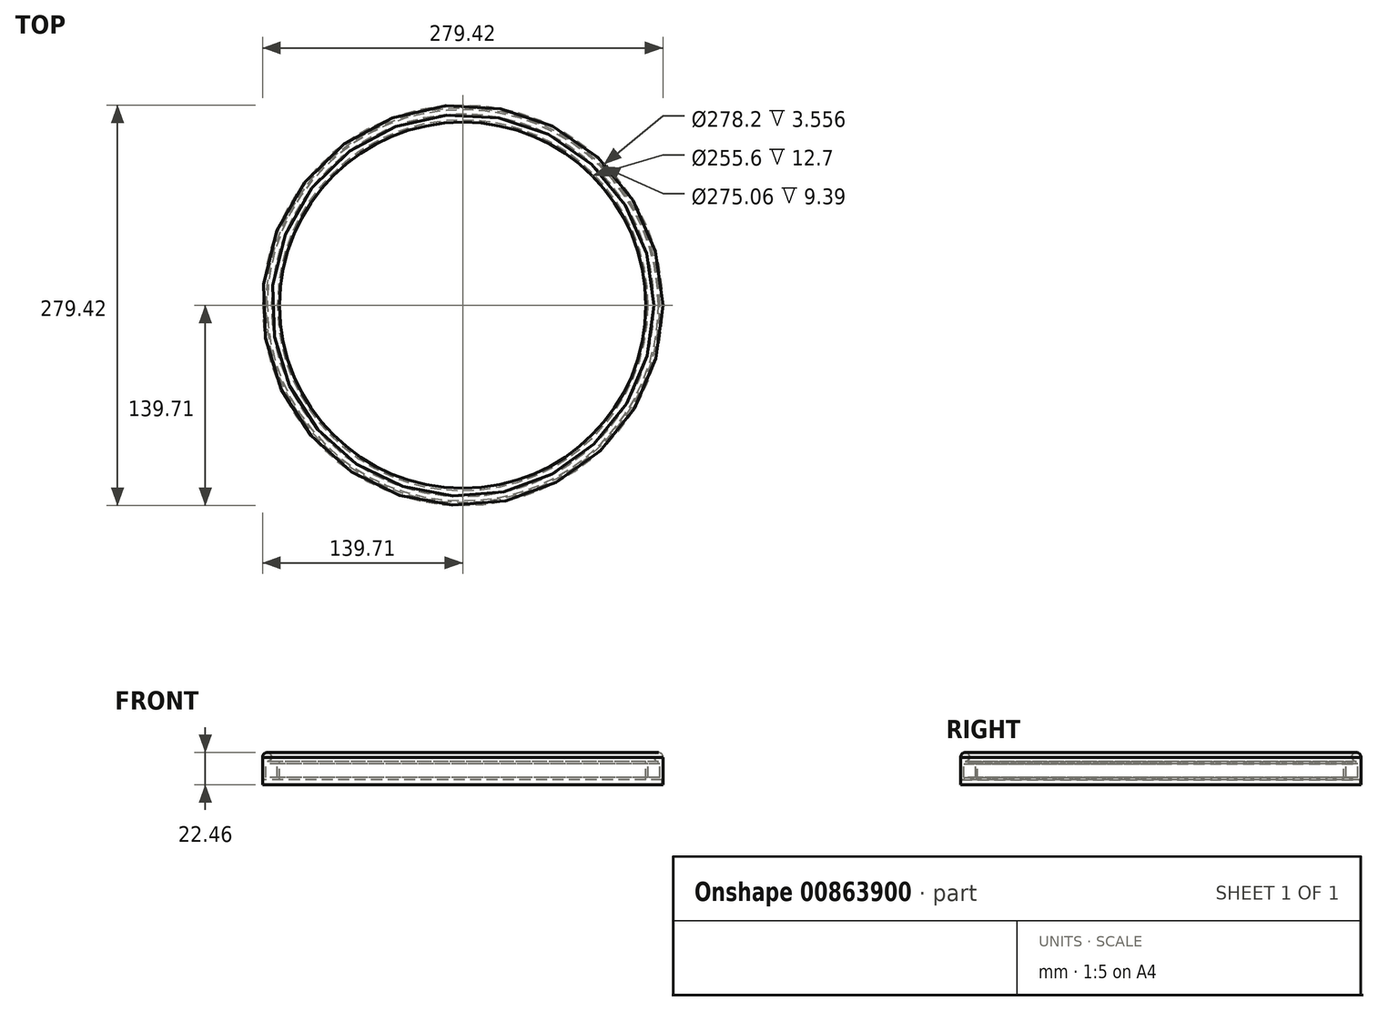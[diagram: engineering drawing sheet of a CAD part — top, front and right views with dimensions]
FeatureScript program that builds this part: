
annotation { "Feature Type Name" : "Feature", "Feature Type Description" : "" }
export const myFeature = defineFeature(function(context is Context, id is Id, definition is map)
    precondition{}
    {
        {
            var Q0;
            Q0=qCreatedBy(makeId("Front.planeOp"),FACE);
            var sketch = newSketch(context, id + "F0", { "sketchPlane" : qUnion([Q0])});
            skLineSegment(sketch, "E0", {"start": v(0, 0) * mm, "end": v(0, 19) * mm});
            skArc(sketch, "E1", {"start": v(6.38, 19.04) * mm, "mid": v(3.17, 22.46) * mm, "end": v(0, 19) * mm});
            skLineSegment(sketch, "E2.1", {"start": v(0.6, 0) * mm, "end": v(0.6, 3.56) * mm});
            skLineSegment(sketch, "E3.bottom", {"start": v(2.17, 14.52) * mm, "end": v(10.39, 14.52) * mm});
            skLineSegment(sketch, "E3.top", {"start": v(2.17, 5.13) * mm, "end": v(10.39, 5.13) * mm});
            skLineSegment(sketch, "E3.left", {"start": v(2.17, 14.52) * mm, "end": v(2.17, 5.13) * mm});
            skLineSegment(sketch, "E3.right", {"start": v(10.39, 14.52) * mm, "end": v(10.39, 5.13) * mm});
            skLineSegment(sketch, "E4", {"start": v(0, 0) * mm, "end": v(0.6, 0) * mm});
            skLineSegment(sketch, "E5", {"start": v(139.7, 36.6) * mm, "end": v(139.7, -48.18) * mm, "construction": true});
            skPoint(sketch, "E6.orphan", {"position": v(6.38, 19) * mm});
            skPoint(sketch, "E7.startSnap0", {"position": v(3.17, 22.46) * mm});
            skLineSegment(sketch, "E8", {"start": v(0, 0) * mm, "end": v(0, 34.45) * mm, "construction": true});
            skArc(sketch, "E9", {"start": v(3.24, 16.26) * mm, "mid": v(5.25, 17.08) * mm, "end": v(6.18, 19.04) * mm});
            skLineSegment(sketch, "E10", {"start": v(6.38, 19.04) * mm, "end": v(6.18, 19.04) * mm});
            skLineSegment(sketch, "E11.bottom", {"start": v(0.6, 3.56) * mm, "end": v(11.9, 3.56) * mm});
            skLineSegment(sketch, "E11.top", {"start": v(3.24, 16.26) * mm, "end": v(11.9, 16.26) * mm});
            skLineSegment(sketch, "E11.right", {"start": v(11.9, 3.56) * mm, "end": v(11.9, 16.26) * mm});
            skSolve(sketch);
        }
        {
            var Q0;
            {var subQ3=sQuery(id+"F0.wireOp",EDGE,"D4vTecVY-vFpe-xj6n-Qpqz-vI6iJZ4cA4yG.bottom");Q0=makeQuery(id+"F0.imprint","IMPRINT",FACE,{"disambiguationData":[TD([[makeQuery(id+"F0.imprint","IMPRINT",EDGE,{"derivedFrom":subQ3}),-1.0]])]});}
            var Q1;
            Q1=makeQuery(id+"F0.imprint","IMPRINT",FACE,{"disambiguationData":[TD([[makeQuery(id+"F0.imprint","IMPRINT",EDGE,{"derivedFrom":sQuery(id+"F0.wireOp",EDGE,"E0")}),-1.0]])]});
            var Q2;
            Q2=sQuery(id+"F0.wireOp",EDGE,"E4");
            var Q3;
            Q3=sQuery(id+"F0.wireOp",EDGE,"E1");
            var Q4;
            Q4=sQuery(id+"F0.wireOp",EDGE,"E2.0");
            var Q5;
            Q5=sQuery(id+"F0.wireOp",EDGE,"E0");
            var Q6;
            Q6=sQuery(id+"F0.wireOp",EDGE,"E2.1");
            var Q7;
            Q7=sQuery(id+"F0.wireOp",EDGE,"ZPap1eRQ-jWB4-mbMz-b1mi-PDOdVzlIXgIv");
            var Q8;
            Q8=sQuery(id+"F0.wireOp",EDGE,"E5");
            revolve(context, id + "F1", {"surfaceOperationType" : NewSurfaceOperationType.NEW, "entities" : qUnion([Q0, Q1]), "surfaceEntities" : qUnion([Q2, Q3, Q4, Q5, Q6, Q7]), "axis" : qUnion([Q8]), "revolveType" : RevolveType.FULL});
        }
    });
